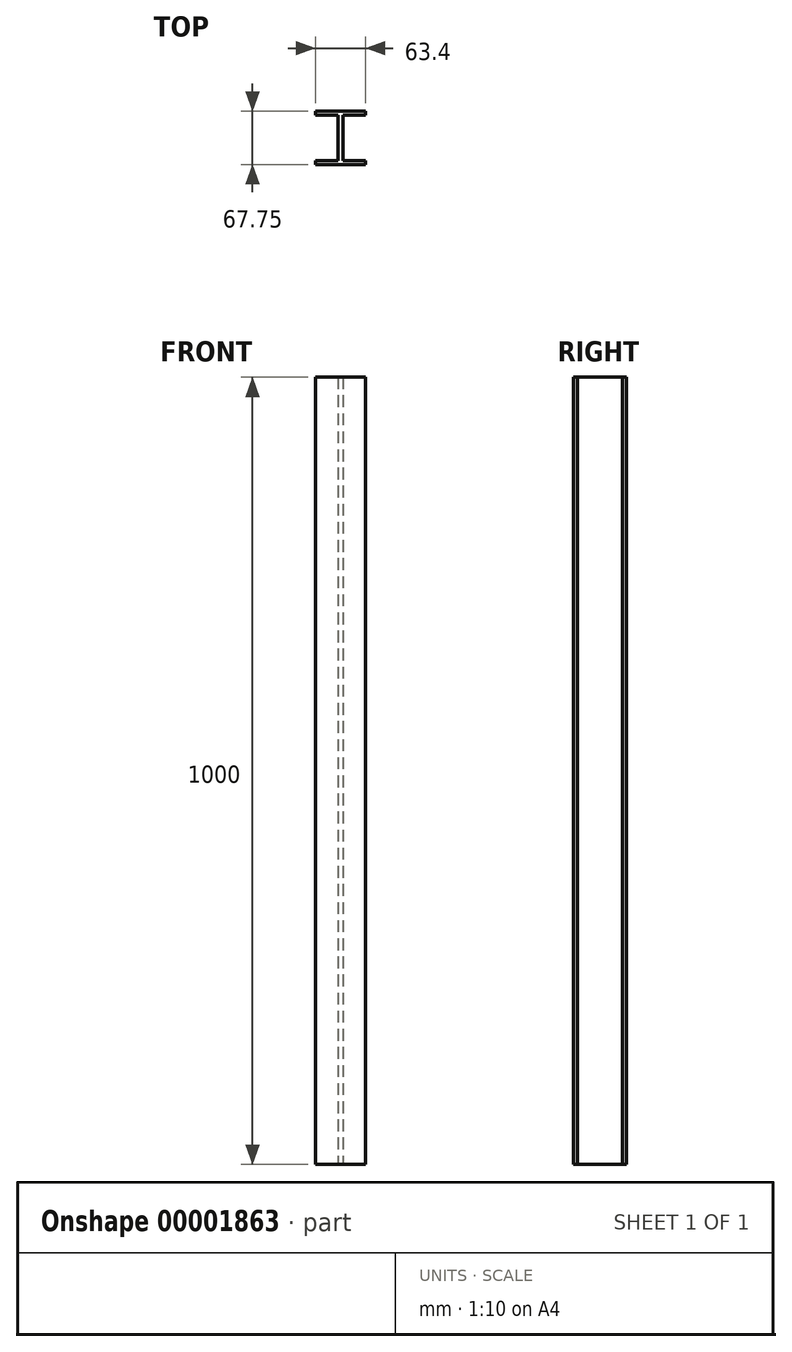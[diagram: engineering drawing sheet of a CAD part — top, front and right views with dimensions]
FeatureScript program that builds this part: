
annotation { "Feature Type Name" : "Feature", "Feature Type Description" : "" }
export const myFeature = defineFeature(function(context is Context, id is Id, definition is map)
    precondition{}
    {
        {
            var Q0;
            Q0=qCreatedBy(makeId("Top.planeOp"),FACE);
            var sketch = newSketch(context, id + "F0", { "sketchPlane" : qUnion([Q0])});
            skLineSegment(sketch, "E0", {"start": v(-31.7, 24.64) * mm, "end": v(31.7, 24.64) * mm});
            skLineSegment(sketch, "E1", {"start": v(31.7, 24.64) * mm, "end": v(31.7, 19.57) * mm});
            skLineSegment(sketch, "E2", {"start": v(31.7, 19.57) * mm, "end": v(3, 19.57) * mm});
            skLineSegment(sketch, "E3", {"start": v(3, 19.57) * mm, "end": v(3, -38.04) * mm});
            skLineSegment(sketch, "E4", {"start": v(3, -38.04) * mm, "end": v(31.7, -38.04) * mm});
            skLineSegment(sketch, "E5", {"start": v(31.7, -38.04) * mm, "end": v(31.7, -43.11) * mm});
            skLineSegment(sketch, "E6", {"start": v(31.7, -43.11) * mm, "end": v(-31.7, -43.11) * mm});
            skLineSegment(sketch, "E7", {"start": v(-31.7, -43.11) * mm, "end": v(-31.7, -38.04) * mm});
            skLineSegment(sketch, "E8", {"start": v(-31.7, -38.04) * mm, "end": v(-3, -38.04) * mm});
            skLineSegment(sketch, "E9", {"start": v(-3, -38.04) * mm, "end": v(-3, 19.57) * mm});
            skLineSegment(sketch, "E10", {"start": v(-3, 19.57) * mm, "end": v(-31.7, 19.57) * mm});
            skLineSegment(sketch, "E11", {"start": v(-31.7, 19.57) * mm, "end": v(-31.7, 24.64) * mm});
            skLineSegment(sketch, "E12", {"start": v(0, 0) * mm, "end": v(0, 44.8) * mm, "construction": true});
            skSolve(sketch);
        }
        {
            var Q0;
            Q0 = qSketchRegion(id + "F0", true);
            extrude(context, id + "F1", {"entities" : qUnion([Q0]), "depth" : 1000 * mm});
        }
    });
